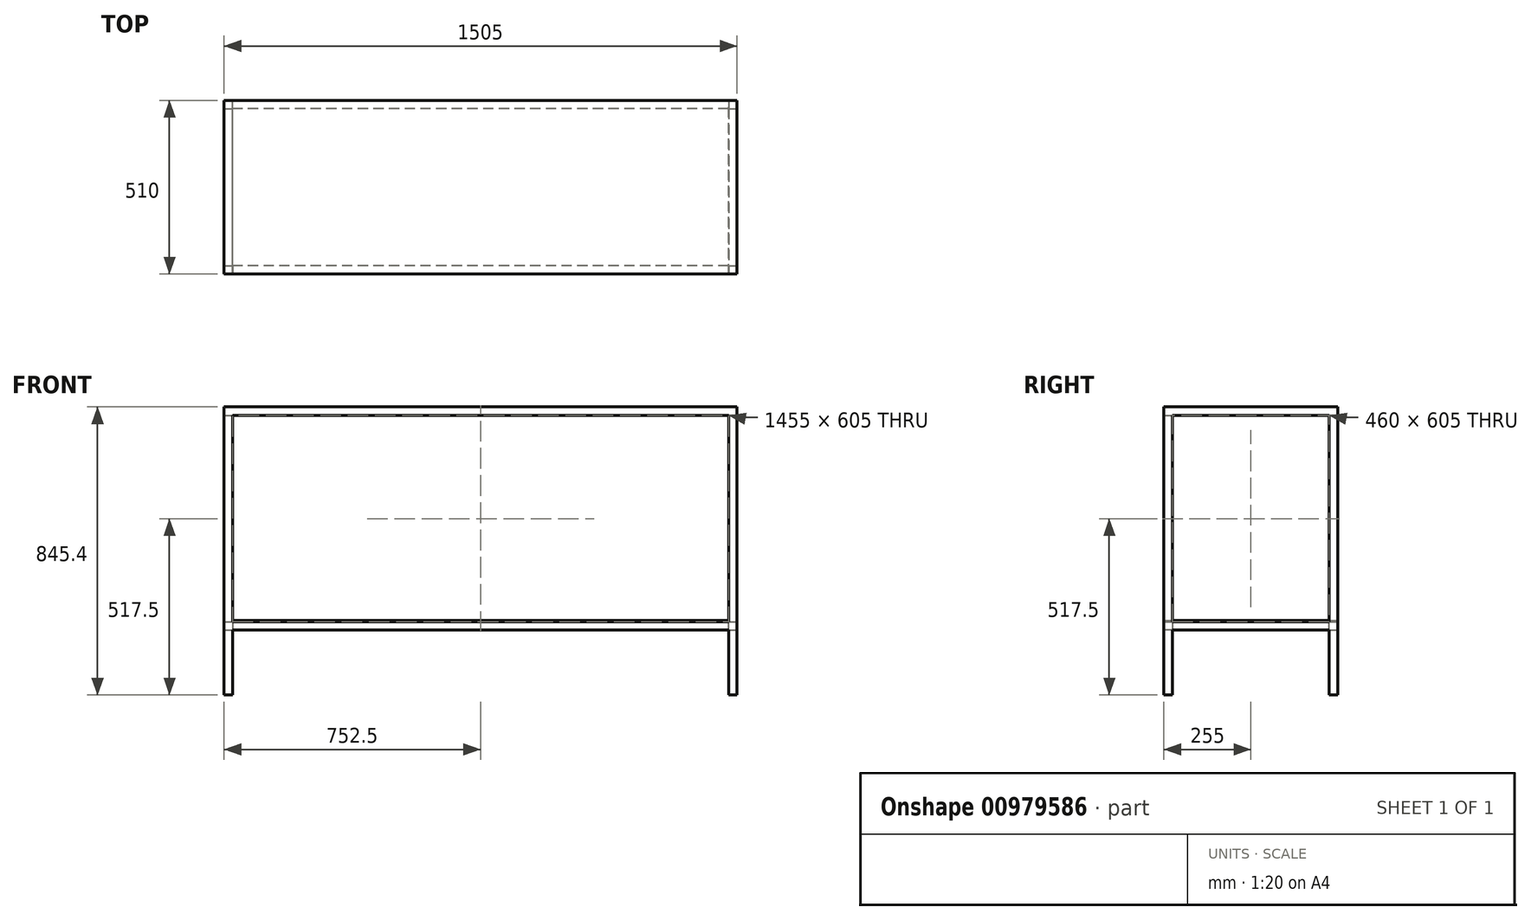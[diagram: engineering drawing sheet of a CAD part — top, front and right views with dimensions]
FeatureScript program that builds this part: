
annotation { "Feature Type Name" : "Feature", "Feature Type Description" : "" }
export const myFeature = defineFeature(function(context is Context, id is Id, definition is map)
    precondition{}
    {
        {
            var Q0;
            Q0=qCreatedBy(makeId("Top.planeOp"),FACE);
            var sketch = newSketch(context, id + "F0", { "sketchPlane" : qUnion([Q0])});
            skLineSegment(sketch, "E0.bottom", {"start": v(752.5, -255) * mm, "end": v(-752.5, -255) * mm});
            skLineSegment(sketch, "E0.top", {"start": v(752.5, 255) * mm, "end": v(-752.5, 255) * mm});
            skLineSegment(sketch, "E0.left", {"start": v(752.5, -255) * mm, "end": v(752.5, 255) * mm});
            skLineSegment(sketch, "E0.right", {"start": v(-752.5, -255) * mm, "end": v(-752.5, 255) * mm});
            skPoint(sketch, "E0.middle", {"position": v(0, 0) * mm});
            skSolve(sketch);
        }
        {
            var Q0;
            Q0 = qSketchRegion(id + "F0", true);
            extrude(context, id + "F1", {"entities" : qUnion([Q0]), "depth" : 25.4 * mm, "offsetDistance" : 25.4 * mm});
        }
        {
            var Q0;
            Q0=makeQuery(id+"F1.opExtrude","CAP_FACE",FACE,{"disambiguationData":[OSD([sQuery(id+"F0.wireOp",EDGE,"E0.bottom"),sQuery(id+"F0.wireOp",EDGE,"E0.top"),sQuery(id+"F0.wireOp",EDGE,"E0.left"),sQuery(id+"F0.wireOp",EDGE,"E0.right")])],"isStart":true});
            var sketch = newSketch(context, id + "F2", { "sketchPlane" : qUnion([Q0])});
            skLineSegment(sketch, "E1.bottom", {"start": v(-752.5, 255) * mm, "end": v(-727.5, 255) * mm});
            skLineSegment(sketch, "E1.top", {"start": v(-752.5, 230) * mm, "end": v(-727.5, 230) * mm});
            skLineSegment(sketch, "E1.left", {"start": v(-752.5, 255) * mm, "end": v(-752.5, 230) * mm});
            skLineSegment(sketch, "E1.right", {"start": v(-727.5, 255) * mm, "end": v(-727.5, 230) * mm});
            skLineSegment(sketch, "E2.bottom", {"start": v(-752.5, -255) * mm, "end": v(-727.5, -255) * mm});
            skLineSegment(sketch, "E2.top", {"start": v(-752.5, -230) * mm, "end": v(-727.5, -230) * mm});
            skLineSegment(sketch, "E2.left", {"start": v(-752.5, -255) * mm, "end": v(-752.5, -230) * mm});
            skLineSegment(sketch, "E2.right", {"start": v(-727.5, -255) * mm, "end": v(-727.5, -230) * mm});
            skLineSegment(sketch, "E3.bottom", {"start": v(752.5, 255) * mm, "end": v(727.5, 255) * mm});
            skLineSegment(sketch, "E3.top", {"start": v(752.5, 230) * mm, "end": v(727.5, 230) * mm});
            skLineSegment(sketch, "E3.left", {"start": v(752.5, 255) * mm, "end": v(752.5, 230) * mm});
            skLineSegment(sketch, "E3.right", {"start": v(727.5, 255) * mm, "end": v(727.5, 230) * mm});
            skLineSegment(sketch, "E4.bottom", {"start": v(752.5, -255) * mm, "end": v(727.5, -255) * mm});
            skLineSegment(sketch, "E4.top", {"start": v(752.5, -230) * mm, "end": v(727.5, -230) * mm});
            skLineSegment(sketch, "E4.left", {"start": v(752.5, -255) * mm, "end": v(752.5, -230) * mm});
            skLineSegment(sketch, "E4.right", {"start": v(727.5, -255) * mm, "end": v(727.5, -230) * mm});
            skSolve(sketch);
        }
        {
            var Q0;
            Q0 = qSketchRegion(id + "F2", true);
            extrude(context, id + "F3", {"entities" : qUnion([Q0]), "operationType" : NewBodyOperationType.ADD, "depth" : 820 * mm, "offsetDistance" : 25.4 * mm});
        }
        {
            var Q0;
            Q0=makeQuery(id+"F3.opExtrude","SWEPT_FACE",FACE,{"disambiguationData":[OSD([sQuery(id+"F2.wireOp",EDGE,"E2.top")])]});
            var sketch = newSketch(context, id + "F4", { "sketchPlane" : qUnion([Q0])});
            skLineSegment(sketch, "E5.bottom", {"start": v(-752.5, -605) * mm, "end": v(-727.5, -605) * mm});
            skLineSegment(sketch, "E5.top", {"start": v(-752.5, -630) * mm, "end": v(-727.5, -630) * mm});
            skLineSegment(sketch, "E5.left", {"start": v(-752.5, -605) * mm, "end": v(-752.5, -630) * mm});
            skLineSegment(sketch, "E5.right", {"start": v(-727.5, -605) * mm, "end": v(-727.5, -630) * mm});
            skSolve(sketch);
        }
        {
            var Q0;
            Q0 = qSketchRegion(id + "F4", true);
            extrude(context, id + "F5", {"entities" : qUnion([Q0]), "operationType" : NewBodyOperationType.ADD, "endBound" : BoundingType.UP_TO_NEXT, "depth" : 25.4 * mm, "offsetDistance" : 25.4 * mm});
        }
        {
            var Q0;
            Q0=makeQuery(id+"F5.boolean.opBoolean","MERGE",FACE,{"derivedFrom":[makeQuery(id+"F3.opExtrude","SWEPT_FACE",FACE,{"disambiguationData":[OSD([sQuery(id+"F2.wireOp",EDGE,"E1.right")])]}),makeQuery(id+"F3.opExtrude","SWEPT_FACE",FACE,{"disambiguationData":[OSD([sQuery(id+"F2.wireOp",EDGE,"E2.right")])]}),makeQuery(id+"F5.opExtrude","SWEPT_FACE",FACE,{"disambiguationData":[OSD([sQuery(id+"F4.wireOp",EDGE,"E5.right")])]})]});
            var sketch = newSketch(context, id + "F6", { "sketchPlane" : qUnion([Q0])});
            skLineSegment(sketch, "E6.bottom", {"start": v(-230, -605) * mm, "end": v(-255, -605) * mm});
            skLineSegment(sketch, "E6.top", {"start": v(-230, -630) * mm, "end": v(-255, -630) * mm});
            skLineSegment(sketch, "E6.left", {"start": v(-230, -605) * mm, "end": v(-230, -630) * mm});
            skLineSegment(sketch, "E6.right", {"start": v(-255, -605) * mm, "end": v(-255, -630) * mm});
            skSolve(sketch);
        }
        {
            var Q0;
            Q0 = qSketchRegion(id + "F6", true);
            extrude(context, id + "F7", {"entities" : qUnion([Q0]), "operationType" : NewBodyOperationType.ADD, "endBound" : BoundingType.UP_TO_NEXT, "depth" : 25.4 * mm, "offsetDistance" : 25.4 * mm});
        }
        {
            var Q0;
            Q0=makeQuery(id+"F7.boolean.opBoolean","MERGE",FACE,{"derivedFrom":[makeQuery(id+"F3.opExtrude","SWEPT_FACE",FACE,{"disambiguationData":[OSD([sQuery(id+"F2.wireOp",EDGE,"E3.top")])]}),makeQuery(id+"F7.opExtrude","SWEPT_FACE",FACE,{"disambiguationData":[OSD([sQuery(id+"F6.wireOp",EDGE,"E6.left")])]})]});
            var sketch = newSketch(context, id + "F8", { "sketchPlane" : qUnion([Q0])});
            skLineSegment(sketch, "E7.bottom", {"start": v(-727.5, -605) * mm, "end": v(-752.5, -605) * mm});
            skLineSegment(sketch, "E7.top", {"start": v(-727.5, -630) * mm, "end": v(-752.5, -630) * mm});
            skLineSegment(sketch, "E7.left", {"start": v(-727.5, -605) * mm, "end": v(-727.5, -630) * mm});
            skLineSegment(sketch, "E7.right", {"start": v(-752.5, -605) * mm, "end": v(-752.5, -630) * mm});
            skSolve(sketch);
        }
        {
            var Q0;
            Q0 = qSketchRegion(id + "F8", true);
            extrude(context, id + "F9", {"entities" : qUnion([Q0]), "operationType" : NewBodyOperationType.ADD, "endBound" : BoundingType.UP_TO_NEXT, "depth" : 25.4 * mm, "offsetDistance" : 25.4 * mm});
        }
        {
            var Q0;
            {var subQ0=makeQuery(id+"F5.opExtrude","SWEPT_FACE",FACE,{"disambiguationData":[OSD([sQuery(id+"F4.wireOp",EDGE,"E5.right")])]});var subQ1=sQuery(id+"F2.wireOp",EDGE,"E2.top");var subQ2=sQuery(id+"F2.wireOp",EDGE,"E2.right");var subQ3=sQuery(id+"F2.wireOp",EDGE,"E2.bottom");var subQ4=makeQuery(id+"F3.opExtrude","SWEPT_FACE",FACE,{"disambiguationData":[OSD([subQ2])]});var subQ5=sQuery(id+"F0.wireOp",EDGE,"E0.top");var subQ6=makeQuery(id+"F3.opExtrude","SWEPT_FACE",FACE,{"disambiguationData":[OSD([sQuery(id+"F2.wireOp",EDGE,"E1.right")])]});Q0=makeQuery(id+"F7.boolean.opBoolean","SPLIT",FACE,{"disambiguationData":[TD([makeQuery(id+"F1.opExtrude","CAP_FACE",FACE,{"disambiguationData":[OSD([sQuery(id+"F0.wireOp",EDGE,"E0.bottom"),subQ5,sQuery(id+"F0.wireOp",EDGE,"E0.left"),sQuery(id+"F0.wireOp",EDGE,"E0.right")])],"isStart":true}),makeQuery(id+"F1.opExtrude","SWEPT_FACE",FACE,{"disambiguationData":[OSD([subQ5])]}),makeQuery(id+"F3.opExtrude","SWEPT_FACE",FACE,{"disambiguationData":[OSD([sQuery(id+"F2.wireOp",EDGE,"E1.top")])]}),subQ6,makeQuery(id+"F3.opExtrude","SWEPT_FACE",FACE,{"disambiguationData":[OSD([subQ3])]}),makeQuery(id+"F3.opExtrude","CAP_FACE",FACE,{"disambiguationData":[OSD([subQ3,subQ1,sQuery(id+"F2.wireOp",EDGE,"E2.left"),subQ2])],"isStart":false}),makeQuery(id+"F3.opExtrude","SWEPT_FACE",FACE,{"disambiguationData":[OSD([subQ1])]}),subQ4,makeQuery(id+"F3.opExtrude","SWEPT_FACE",FACE,{"disambiguationData":[OSD([sQuery(id+"F2.wireOp",EDGE,"E3.top")])]}),makeQuery(id+"F3.opExtrude","SWEPT_FACE",FACE,{"disambiguationData":[OSD([sQuery(id+"F2.wireOp",EDGE,"E4.bottom")])]}),makeQuery(id+"F5.opExtrude","SWEPT_FACE",FACE,{"disambiguationData":[OSD([sQuery(id+"F4.wireOp",EDGE,"E5.bottom")])]}),makeQuery(id+"F5.opExtrude","SWEPT_FACE",FACE,{"disambiguationData":[OSD([sQuery(id+"F4.wireOp",EDGE,"E5.top")])]}),subQ0,makeQuery(id+"F7.opExtrude","SWEPT_FACE",FACE,{"disambiguationData":[OSD([sQuery(id+"F6.wireOp",EDGE,"E6.bottom")])]}),makeQuery(id+"F7.opExtrude","SWEPT_FACE",FACE,{"disambiguationData":[OSD([sQuery(id+"F6.wireOp",EDGE,"E6.top")])]}),makeQuery(id+"F7.opExtrude","SWEPT_FACE",FACE,{"disambiguationData":[OSD([sQuery(id+"F6.wireOp",EDGE,"E6.left")])]})])],"derivedFrom":makeQuery(id+"F5.boolean.opBoolean","MERGE",FACE,{"derivedFrom":[subQ6,subQ4,subQ0]})});}
            var sketch = newSketch(context, id + "F10", { "sketchPlane" : qUnion([Q0])});
            skLineSegment(sketch, "E8.bottom", {"start": v(230, -605) * mm, "end": v(255, -605) * mm});
            skLineSegment(sketch, "E8.top", {"start": v(230, -630) * mm, "end": v(255, -630) * mm});
            skLineSegment(sketch, "E8.left", {"start": v(230, -605) * mm, "end": v(230, -630) * mm});
            skLineSegment(sketch, "E8.right", {"start": v(255, -605) * mm, "end": v(255, -630) * mm});
            skSolve(sketch);
        }
        {
            var Q0;
            Q0 = qSketchRegion(id + "F10", true);
            extrude(context, id + "F11", {"entities" : qUnion([Q0]), "operationType" : NewBodyOperationType.ADD, "endBound" : BoundingType.UP_TO_NEXT, "depth" : 25.4 * mm, "offsetDistance" : 25.4 * mm});
        }
        {
            var Q0;
            Q0=makeQuery(id+"F5.opExtrude","SWEPT_FACE",FACE,{"disambiguationData":[OSD([sQuery(id+"F4.wireOp",EDGE,"E5.bottom")])]});
            var sketch = newSketch(context, id + "F12", { "sketchPlane" : qUnion([Q0])});
            skLineSegment(sketch, "E9.bottom", {"start": v(-727.5, -255) * mm, "end": v(727.5, -255) * mm});
            skLineSegment(sketch, "E9.top", {"start": v(-727.5, 255) * mm, "end": v(727.5, 255) * mm});
            skLineSegment(sketch, "E9.left", {"start": v(-727.5, -255) * mm, "end": v(-727.5, 255) * mm});
            skLineSegment(sketch, "E9.right", {"start": v(727.5, -255) * mm, "end": v(727.5, 255) * mm});
            skSolve(sketch);
        }
        {
            var Q0;
            Q0 = qSketchRegion(id + "F12", true);
            extrude(context, id + "F13", {"entities" : qUnion([Q0]), "depth" : 3 * mm, "offsetDistance" : 25.4 * mm});
        }
    });
